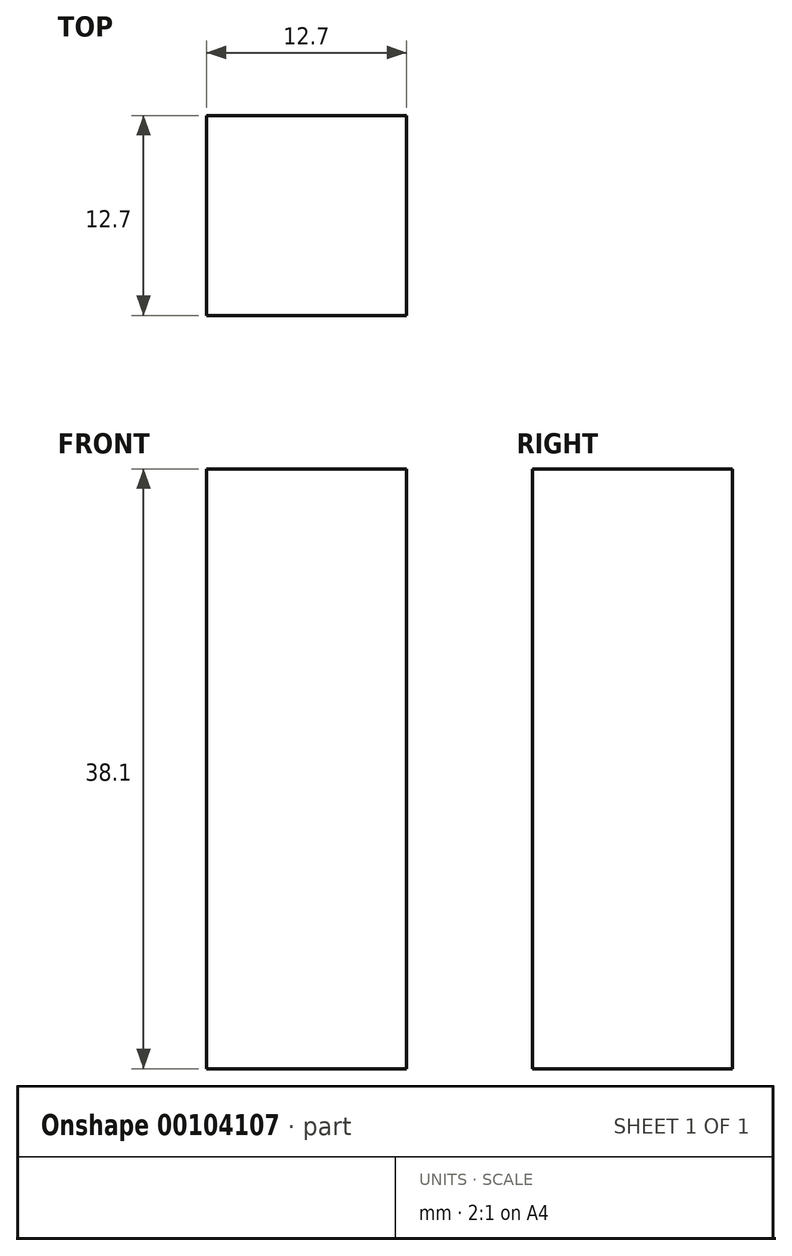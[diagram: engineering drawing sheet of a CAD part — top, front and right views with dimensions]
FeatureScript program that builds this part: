
annotation { "Feature Type Name" : "Feature", "Feature Type Description" : "" }
export const myFeature = defineFeature(function(context is Context, id is Id, definition is map)
    precondition{}
    {
        {
            var Q0;
            Q0=qCreatedBy(makeId("Front.planeOp"),FACE);
            var sketch = newSketch(context, id + "F0", { "sketchPlane" : qUnion([Q0])});
            skLineSegment(sketch, "E0.bottom", {"start": v(-15.05, -23.56) * mm, "end": v(-2.35, -23.56) * mm});
            skLineSegment(sketch, "E0.top", {"start": v(-15.05, -61.66) * mm, "end": v(-2.35, -61.66) * mm});
            skLineSegment(sketch, "E0.left", {"start": v(-15.05, -23.56) * mm, "end": v(-15.05, -61.66) * mm});
            skLineSegment(sketch, "E0.right", {"start": v(-2.35, -23.56) * mm, "end": v(-2.35, -61.66) * mm});
            skSolve(sketch);
        }
        {
            var Q0;
            Q0=makeQuery(id+"F0.imprint","IMPRINT",FACE,{"disambiguationData":[TD([[makeQuery(id+"F0.imprint","IMPRINT",EDGE,{"derivedFrom":sQuery(id+"F0.wireOp",EDGE,"E0.bottom")}),-1.0]])]});
            extrude(context, id + "F1", {"entities" : qUnion([Q0]), "depth" : 12.7 * mm});
        }
    });
